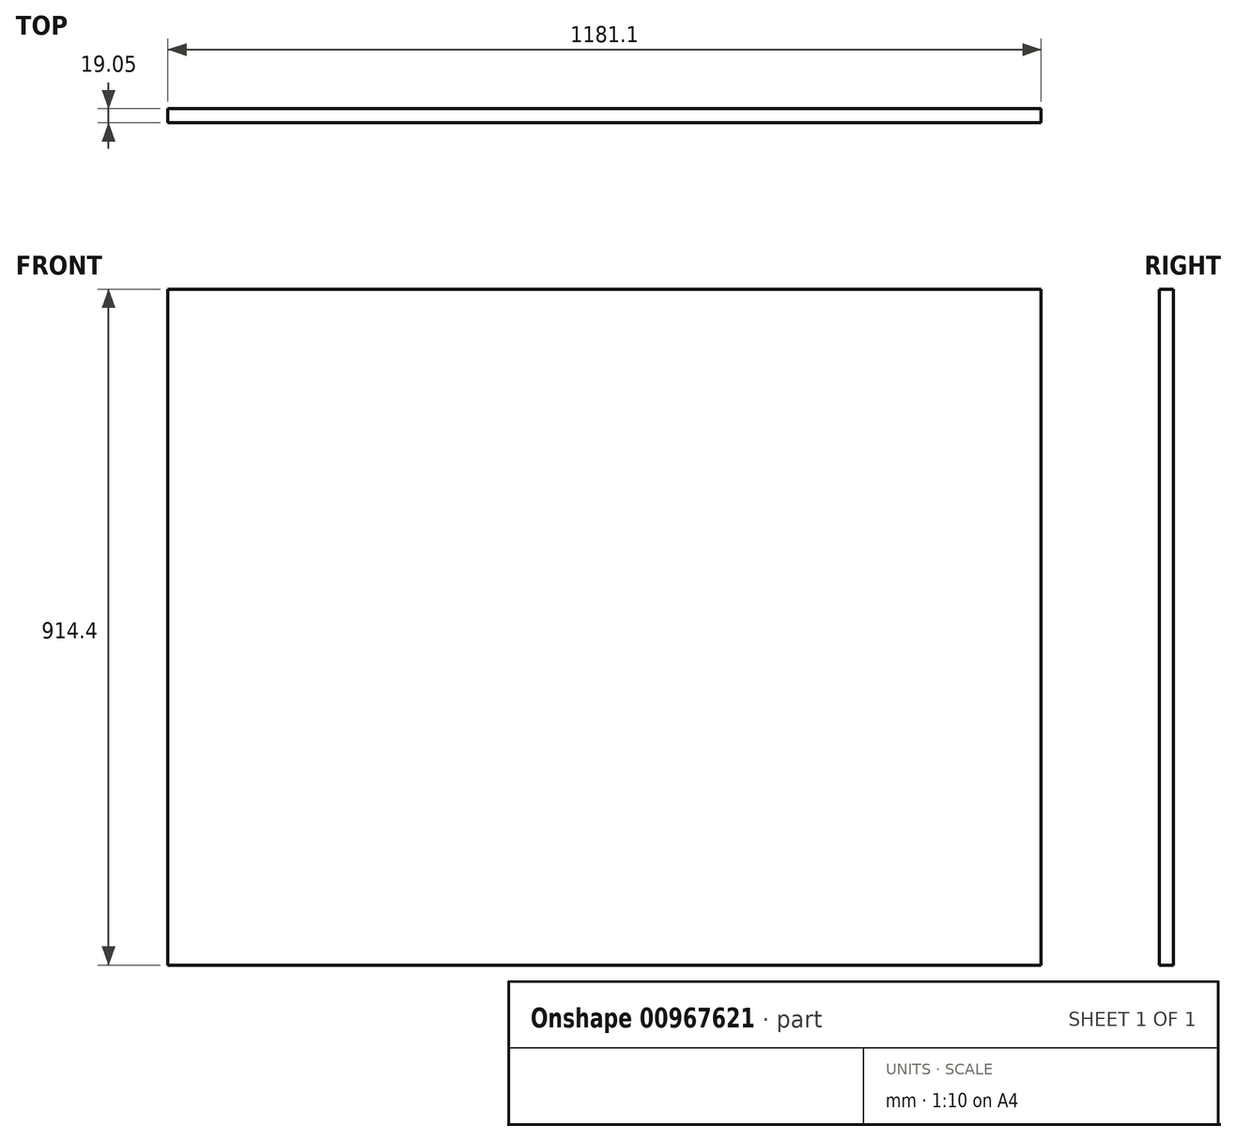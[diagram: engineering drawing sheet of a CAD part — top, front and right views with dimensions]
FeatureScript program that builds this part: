
annotation { "Feature Type Name" : "Feature", "Feature Type Description" : "" }
export const myFeature = defineFeature(function(context is Context, id is Id, definition is map)
    precondition{}
    {
        {
            var Q0;
            Q0=qCreatedBy(makeId("Front.planeOp"),FACE);
            var sketch = newSketch(context, id + "F0", { "sketchPlane" : qUnion([Q0])});
            skLineSegment(sketch, "E0.bottom", {"start": v(590.55, 457.2) * mm, "end": v(-590.55, 457.2) * mm});
            skLineSegment(sketch, "E0.top", {"start": v(590.55, -457.2) * mm, "end": v(-590.55, -457.2) * mm});
            skLineSegment(sketch, "E0.left", {"start": v(590.55, 457.2) * mm, "end": v(590.55, -457.2) * mm});
            skLineSegment(sketch, "E0.right", {"start": v(-590.55, 457.2) * mm, "end": v(-590.55, -457.2) * mm});
            skPoint(sketch, "E0.middle", {"position": v(0, 0) * mm});
            skSolve(sketch);
        }
        {
            var Q0;
            Q0 = qSketchRegion(id + "F0", true);
            extrude(context, id + "F1", {"entities" : qUnion([Q0]), "depth" : 19.05 * mm, "offsetDistance" : 25.4 * mm});
        }
    });
